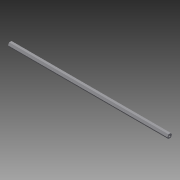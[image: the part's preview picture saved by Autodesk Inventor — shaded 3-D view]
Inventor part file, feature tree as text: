
AUTODESK INVENTOR PART (.ipt)
format: ipt  version: 2015 SP1 (Build 190203100, 203)  size: 86,528 bytes
history: native  units: in
note: dims shown in document units (in); Inventor stores cm internally (conversion verified against a paired STEP export)
features: extrude x2, sketch x2, thread x1
ambient origin geometry x8: Origin, YZ Plane, XZ Plane, XY Plane, X Axis, Y Axis, Z Axis, Center Point
bodies: Solid1 (feature_tree)
feature tree (5):
  extrude  "Extrusion1"  Depth=0.5in
  extrude  "Extrusion2"  Depth=0.5in
  thread  "Thread1"  [1 undecoded]
  sketch  "Sketch1"  dims[d0=0.5in d1=0.5in]
  sketch  "Sketch2"  dims[d2=0.5in d3=0.25in d4=120.0deg d5=120.0deg d6=0.25in d7=0.25in d8=19.625in d9=0.0in d10=0.25in d11=0.5in d12=0.0in d13=1.0in d14=0.0in]
note: 1 required parameter value undecoded (feature->parameter linkage not recoverable at this tier; creation-order binding heuristic only, values carry confidence <= 0.55)
